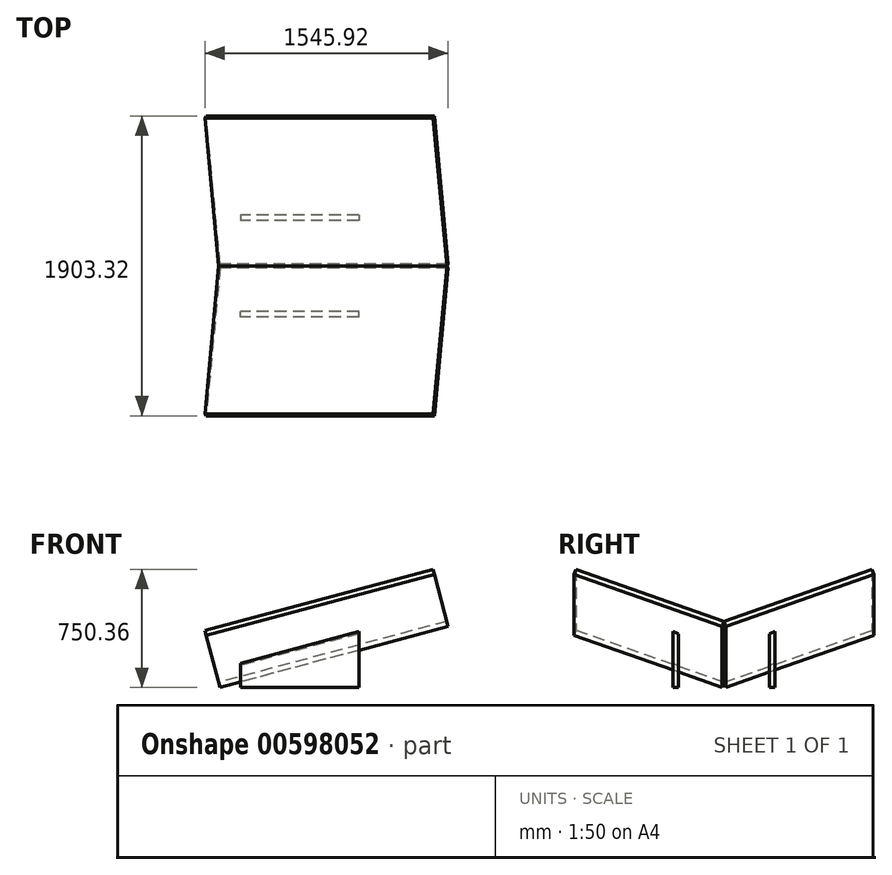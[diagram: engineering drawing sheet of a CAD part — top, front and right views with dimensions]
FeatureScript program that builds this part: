
annotation { "Feature Type Name" : "Feature", "Feature Type Description" : "" }
export const myFeature = defineFeature(function(context is Context, id is Id, definition is map)
    precondition{}
    {
        {
            var Q0;
            Q0=qCreatedBy(makeId("Top.planeOp"),FACE);
            var sketch = newSketch(context, id + "F0", { "sketchPlane" : qUnion([Q0])});
            skLineSegment(sketch, "E0.bottom", {"start": v(0, 0) * mm, "end": v(32.89, -11.97) * mm});
            skLineSegment(sketch, "E0.top", {"start": v(-342.02, -939.7) * mm, "end": v(-309.13, -951.66) * mm});
            skLineSegment(sketch, "E0.left", {"start": v(0, 0) * mm, "end": v(-342.02, -939.7) * mm});
            skLineSegment(sketch, "E0.right", {"start": v(32.89, -11.97) * mm, "end": v(-309.13, -951.66) * mm});
            skLineSegment(sketch, "E1.bottom", {"start": v(-309.13, 951.66) * mm, "end": v(-342.02, 939.7) * mm});
            skLineSegment(sketch, "E1.top", {"start": v(32.89, 11.97) * mm, "end": v(0, 0) * mm});
            skLineSegment(sketch, "E1.left", {"start": v(32.89, 11.97) * mm, "end": v(-309.13, 951.66) * mm});
            skLineSegment(sketch, "E1.right", {"start": v(0, 0) * mm, "end": v(-342.02, 939.7) * mm});
            skPoint(sketch, "E2.endSnap0", {"position": v(16.44, 5.99) * mm});
            skLineSegment(sketch, "E3", {"start": v(32.89, -599.51) * mm, "end": v(32.89, 759.35) * mm, "construction": true});
            skSolve(sketch);
        }
        {
            var Q0;
            Q0 = qSketchRegion(id + "F0", true);
            extrude(context, id + "F1", {"entities" : qUnion([Q0]), "depth" : 1500 * mm, "offsetDistance" : 25 * mm});
        }
        {
            var Q0;
            Q0=makeQuery(id+"F1.opExtrude","SWEPT_BODY",BODY,{"disambiguationData":[OSD([sQuery(id+"F0.wireOp",EDGE,"E0.bottom"),sQuery(id+"F0.wireOp",EDGE,"E0.top"),sQuery(id+"F0.wireOp",EDGE,"E0.left"),sQuery(id+"F0.wireOp",EDGE,"E0.right")])]});
            var Q1;
            Q1=makeQuery(id+"F1.opExtrude","SWEPT_BODY",BODY,{"disambiguationData":[OSD([sQuery(id+"F0.wireOp",EDGE,"E1.bottom"),sQuery(id+"F0.wireOp",EDGE,"E1.top"),sQuery(id+"F0.wireOp",EDGE,"E1.left"),sQuery(id+"F0.wireOp",EDGE,"E1.right")])]});
            var Q2;
            Q2=sQuery(id+"F0.wireOp",EDGE,"E3");
            var Q3;
            Q3=sQuery(id+"F0.wireOp",EDGE,"E3");
            transform(context, id + "F2", {"entities" : qUnion([Q0, Q1]), "transformType" : TransformType.ROTATION, "transformAxis" : qUnion([Q3]), "angle" : 75 * degree, "makeCopy" : false});
        }
        {
            var Q0;
            Q0=qCreatedBy(makeId("Top.planeOp"),FACE);
            var sketch = newSketch(context, id + "F3", { "sketchPlane" : qUnion([Q0])});
            skLineSegment(sketch, "E4.bottom", {"start": v(164.25, -289.55) * mm, "end": v(915, -289.55) * mm});
            skLineSegment(sketch, "E4.top", {"start": v(164.25, -324.55) * mm, "end": v(915, -324.55) * mm});
            skLineSegment(sketch, "E4.left", {"start": v(164.25, -289.55) * mm, "end": v(164.25, -324.55) * mm});
            skLineSegment(sketch, "E4.right", {"start": v(915, -289.55) * mm, "end": v(915, -324.55) * mm});
            skSolve(sketch);
        }
        {
            var Q0;
            Q0=makeQuery(id+"F3.imprint","IMPRINT",FACE,{"disambiguationData":[TD([[makeQuery(id+"F3.imprint","IMPRINT",EDGE,{"derivedFrom":sQuery(id+"F3.wireOp",EDGE,"E4.bottom")}),-1.0]])]});
            extrude(context, id + "F4", {"entities" : qUnion([Q0]), "endBound" : BoundingType.UP_TO_NEXT, "depth" : 25 * mm, "offsetDistance" : 25 * mm});
        }
        {
            var Q0;
            Q0=makeQuery(id+"F4.opExtrude","SWEPT_BODY",BODY,{"disambiguationData":[OSD([sQuery(id+"F3.wireOp",EDGE,"E4.bottom"),sQuery(id+"F3.wireOp",EDGE,"E4.top"),sQuery(id+"F3.wireOp",EDGE,"E4.left"),sQuery(id+"F3.wireOp",EDGE,"E4.right")])]});
            var Q1;
            Q1=qCreatedBy(makeId("Front.planeOp"),FACE);
            mirror(context, id + "F5", {"operationType" : NewBodyOperationType.ADD, "entities" : qUnion([Q0]), "mirrorPlane" : qUnion([Q1])});
        }
    });
